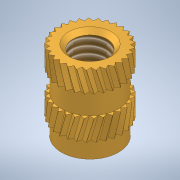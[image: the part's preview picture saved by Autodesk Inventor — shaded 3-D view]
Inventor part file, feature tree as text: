
AUTODESK INVENTOR PART (.ipt)
format: ipt  version: 2022 (Build 260153000, 153)  size: 739,328 bytes
history: native  units: mm
features: sketch x4, revolve x1, loft x1, pattern_circular x1, plane x1, mirror x1, hole x1, chamfer x1, projected_geometry x1
ambient origin geometry x8: Origin, YZ Plane, XZ Plane, XY Plane, X Axis, Y Axis, Z Axis, Center Point
bodies: Solid1 (feature_tree)
feature tree (12):
  revolve  "Revolution1"  [1 undecoded]
  loft  "Loft2"
  pattern_circular  "Circular Pattern2"  Angle=90.0deg  [1 undecoded]
  plane  "Work Plane1"
  mirror  "Mirror1"
  hole  "Hole1"  [1 undecoded]
  chamfer  "Chamfer1"  Distance=0.25mm
  sketch  "Sketch1"  dims[d0=2.3mm d1=5.7mm]
  sketch  "Sketch2"  dims[d2=0.25mm d3=1.5mm]
  projected_geometry  "Projected Loop1"
  sketch  "Sketch3"  dims[d4=1.5mm]
  sketch  "Sketch4"  dims[d5=1.5mm d6=90.0deg d16=0.5mm d17=0.25mm d18=0.5mm d19=0.25mm d20=0.0mm d21=90.0deg d22=0.0mm d23=90.0deg d24=0.1mm d25=0.1mm d26=1.745329mm d30=290.0mm d31=360.0deg d33=2.459mm d34=6.0mm d35=6.3mm d36=2.0mm d37=90.0deg d38=8.0mm d39=20.594885mm d40=0.3mm d41=2.0mm d42=45.0deg]
note: 3 required parameter values undecoded (feature->parameter linkage not recoverable at this tier; creation-order binding heuristic only, values carry confidence <= 0.55)